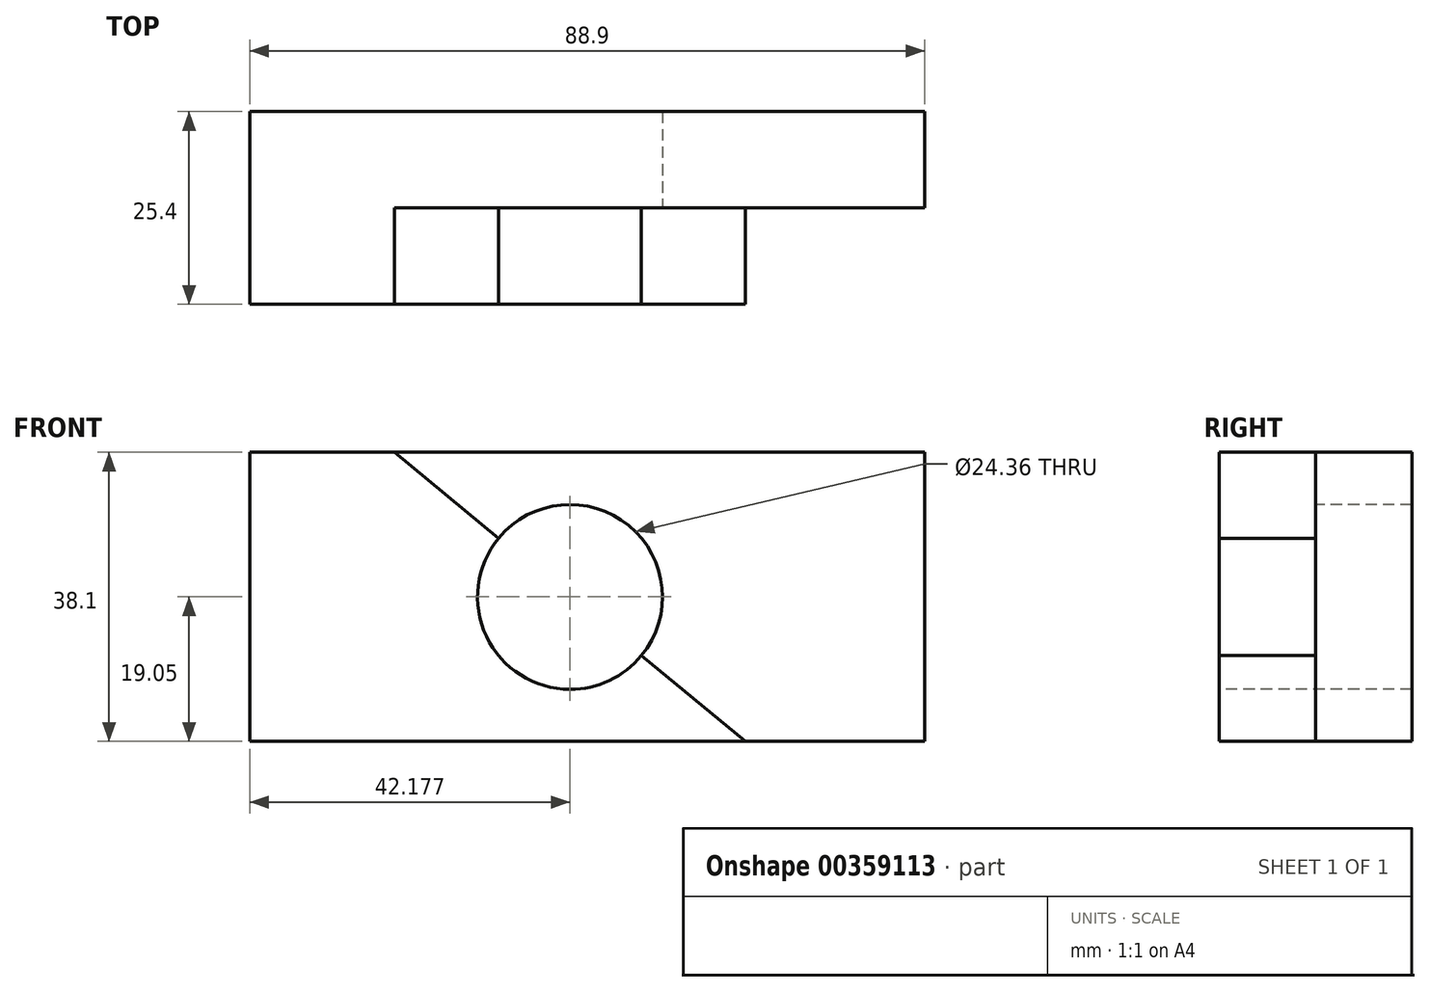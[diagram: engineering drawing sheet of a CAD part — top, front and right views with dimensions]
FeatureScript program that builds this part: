
annotation { "Feature Type Name" : "Feature", "Feature Type Description" : "" }
export const myFeature = defineFeature(function(context is Context, id is Id, definition is map)
    precondition{}
    {
        {
            var Q0;
            Q0=qCreatedBy(makeId("Front.planeOp"),FACE);
            var sketch = newSketch(context, id + "F0", { "sketchPlane" : qUnion([Q0])});
            skLineSegment(sketch, "E0", {"start": v(-65.3, 0) * mm, "end": v(-65.3, 38.1) * mm});
            skLineSegment(sketch, "E1", {"start": v(-65.3, 38.1) * mm, "end": v(23.6, 38.1) * mm});
            skLineSegment(sketch, "E2", {"start": v(23.6, 38.1) * mm, "end": v(23.6, 0) * mm});
            skLineSegment(sketch, "E3", {"start": v(23.6, 0) * mm, "end": v(-65.3, 0) * mm});
            skSolve(sketch);
        }
        {
            var Q0;
            Q0 = qSketchRegion(id + "F0", true);
            extrude(context, id + "F1", {"entities" : qUnion([Q0]), "depth" : 25.4 * mm});
        }
        {
            var Q0;
            Q0=makeQuery(id+"F1.opExtrude","CAP_FACE",FACE,{"disambiguationData":[OSD([sQuery(id+"F0.wireOp",EDGE,"E0"),sQuery(id+"F0.wireOp",EDGE,"E1"),sQuery(id+"F0.wireOp",EDGE,"E2"),sQuery(id+"F0.wireOp",EDGE,"E3")])],"isStart":false});
            var sketch = newSketch(context, id + "F2", { "sketchPlane" : qUnion([Q0])});
            skLineSegment(sketch, "E4", {"start": v(0, 0) * mm, "end": v(-46.25, 38.1) * mm});
            skSolve(sketch);
        }
        {
            var Q0;
            {var subQ0=sQuery(id+"F2.wireOp",EDGE,"E4");Q0=makeQuery(id+"F2.imprint","IMPRINT",FACE,{"disambiguationData":[TD([[makeQuery(id+"F2.imprint","IMPRINT",EDGE,{"derivedFrom":subQ0}),-1.0]])]});}
            extrude(context, id + "F3", {"entities" : qUnion([Q0]), "operationType" : NewBodyOperationType.REMOVE, "oppositeDirection" : true, "depth" : 12.7 * mm});
        }
        {
            var Q0;
            Q0=makeQuery(id+"F1.opExtrude","CAP_FACE",FACE,{"disambiguationData":[OSD([sQuery(id+"F0.wireOp",EDGE,"E0"),sQuery(id+"F0.wireOp",EDGE,"E1"),sQuery(id+"F0.wireOp",EDGE,"E2"),sQuery(id+"F0.wireOp",EDGE,"E3")])],"isStart":false});
            var sketch = newSketch(context, id + "F4", { "sketchPlane" : qUnion([Q0])});
            skCircle(sketch, "E5", {"center": v(-23.12, 19.05) * mm, "radius": 12.18 * mm});
            skSolve(sketch);
        }
        {
            var Q0;
            {var subQ0=sQuery(id+"F4.wireOp",EDGE,"E5");var subQ1=makeQuery(id+"F3.boolean.opBoolean","COPY",EDGE,{"derivedFrom":makeQuery(id+"F3.opExtrude","CAP_EDGE",EDGE,{"disambiguationData":[OSD([sQuery(id+"F2.wireOp",EDGE,"E4")])],"isStart":true})});var subQ2=makeQuery(id+"F4.imprint","INTERSECT",VERTEX,{"disambiguationData":[OD(0.0)],"derivedFrom":[subQ1,subQ0]});Q0=makeQuery(id+"F4.imprint","IMPRINT",FACE,{"disambiguationData":[TD([[makeQuery(id+"F4.imprint","IMPRINT",EDGE,{"disambiguationData":[TD([[subQ2,1.0]])],"derivedFrom":subQ0}),1.0]])]});}
            var Q1;
            {var subQ0=sQuery(id+"F4.wireOp",EDGE,"E5");var subQ1=makeQuery(id+"F3.boolean.opBoolean","COPY",EDGE,{"derivedFrom":makeQuery(id+"F3.opExtrude","CAP_EDGE",EDGE,{"disambiguationData":[OSD([sQuery(id+"F2.wireOp",EDGE,"E4")])],"isStart":true})});var subQ2=makeQuery(id+"F4.imprint","INTERSECT",VERTEX,{"disambiguationData":[OD(0.0)],"derivedFrom":[subQ1,subQ0]});Q1=makeQuery(id+"F4.imprint","IMPRINT",FACE,{"disambiguationData":[TD([[makeQuery(id+"F4.imprint","IMPRINT",EDGE,{"disambiguationData":[TD([[subQ2,-1.0]])],"derivedFrom":subQ0}),1.0]])]});}
            extrude(context, id + "F5", {"entities" : qUnion([Q0, Q1]), "operationType" : NewBodyOperationType.REMOVE, "oppositeDirection" : true, "depth" : 63.5 * mm});
        }
    });
